# Revit family: NLRS_27_GM_LIB_LI_MR
name_source: partatom
category: Generic Models
revit_build: Autodesk Revit 2017 (Build: 20190507_1515(x64)
units: mm (PartAtom-declared; Revit-internal decimal feet)

## family parameters
Can host rebar = No
Cut with Voids When Loaded = Yes
Part Type = Normal
Room Calculation Point = No
Round Connector Dimension = Use Diameter
Shared = No

## types (12) — shared parameters
01_kraal = No
02_Trim = Yes
03_druppel = Yes
Assembly Code = 27.13
Description = LI Luifel
IfcExportAs = IfcFlowsegment
Manufacturer = Meilof Riks
Model = LI
NLRS_C_Binnenbak = RAL 9010
NLRS_C_Materiaal = RAL 9010
Type Image = <None>
URL = https://www.meilofriks.nl

## per-type parameters (varying)
| type | Breedte_goot | Diepte_bak | Hoogte_AK | Hoogte_VK | Set_Diepte_bak | set_Hoogte_AK |
| LI.S365A | 365 mm  [stored 1.19751 ft] | 95 mm | 204 mm  [stored 0.669291 ft] | 176 mm  [stored 0.577428 ft] | 95 mm | 204 mm  [stored 0.669291 ft] |
| LI.S365B | 365 mm  [stored 1.19751 ft] | 95 mm | 254 mm  [stored 0.833333 ft] | 226 mm  [stored 0.74147 ft] | 95 mm | 254 mm  [stored 0.833333 ft] |
| LI.S365C | 365 mm  [stored 1.19751 ft] | 95 mm | 304 mm | 276 mm | 95 mm | 304 mm |
| LI.S400A | 400 mm  [stored 1.31234 ft] | 78 mm  [stored 0.255906 ft] | 186 mm  [stored 0.610236 ft] | 157 mm  [stored 0.515092 ft] | 78 mm  [stored 0.255906 ft] | 186 mm  [stored 0.610236 ft] |
| LI.S450A | 450 mm | 95 mm | 218 mm | 175 mm  [stored 0.574147 ft] | 95 mm | 218 mm |
| LI.S500A | 500 mm  [stored 1.64042 ft] | 78 mm  [stored 0.255906 ft] | 186 mm  [stored 0.610236 ft] | 157 mm  [stored 0.515092 ft] | 78 mm  [stored 0.255906 ft] | 186 mm  [stored 0.610236 ft] |
| LI.S500B | 500 mm  [stored 1.64042 ft] | 78 mm  [stored 0.255906 ft] | 236 mm | 207 mm  [stored 0.679134 ft] | 78 mm  [stored 0.255906 ft] | 236 mm |
| LI.S500C | 500 mm  [stored 1.64042 ft] | 78 mm  [stored 0.255906 ft] | 286 mm | 257 mm | 78 mm  [stored 0.255906 ft] | 286 mm |
| LI.S400B | 400 mm  [stored 1.31234 ft] | 78 mm  [stored 0.255906 ft] | 236 mm | 207 mm  [stored 0.679134 ft] | 78 mm  [stored 0.255906 ft] | 236 mm |
| LI.S400C | 400 mm  [stored 1.31234 ft] | 78 mm  [stored 0.255906 ft] | 286 mm | 257 mm | 78 mm  [stored 0.255906 ft] | 286 mm |
| LI.S450B | 450 mm | 95 mm | 268 mm | 225 mm | 95 mm | 268 mm |
| LI.S450C | 450 mm | 95 mm | 318 mm | 275 mm | 95 mm | 318 mm |

note: [stored X ft] marks values corroborated as IEEE doubles in the binary element streams (Revit-internal decimal feet)

## geometry (parser evidence)
native form markers: Sweep x23
no freeform markers — native parametric forms only
